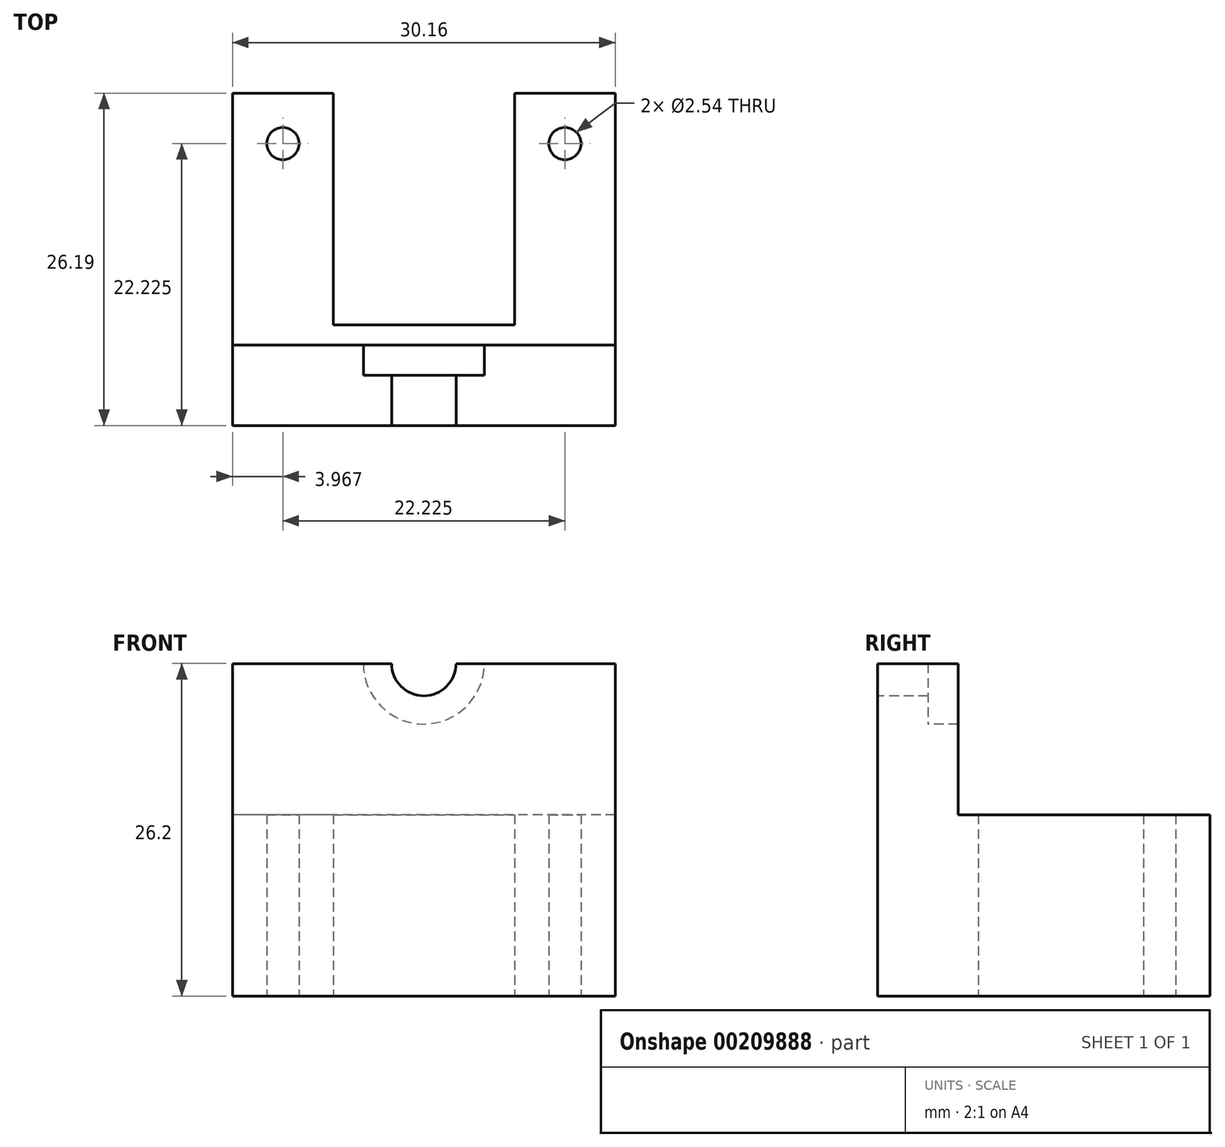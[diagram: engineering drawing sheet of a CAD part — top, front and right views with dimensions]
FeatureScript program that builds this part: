
annotation { "Feature Type Name" : "Feature", "Feature Type Description" : "" }
export const myFeature = defineFeature(function(context is Context, id is Id, definition is map)
    precondition{}
    {
        {
            var Q0;
            Q0=qCreatedBy(makeId("Top.planeOp"),FACE);
            var sketch = newSketch(context, id + "F0", { "sketchPlane" : qUnion([Q0])});
            skLineSegment(sketch, "E0", {"start": v(0, 0) * mm, "end": v(-15.08, 0) * mm});
            skLineSegment(sketch, "E1", {"start": v(-15.08, 0) * mm, "end": v(-15.08, 26.2) * mm});
            skLineSegment(sketch, "E2", {"start": v(-15.08, 26.2) * mm, "end": v(-7.14, 26.2) * mm});
            skLineSegment(sketch, "E3", {"start": v(-7.14, 26.2) * mm, "end": v(-7.14, 7.94) * mm});
            skLineSegment(sketch, "E4", {"start": v(-7.14, 7.94) * mm, "end": v(0, 7.94) * mm});
            skLineSegment(sketch, "E5.MirrorCS", {"start": v(15.08, 26.2) * mm, "end": v(7.14, 26.2) * mm});
            skLineSegment(sketch, "E6.MirrorCS", {"start": v(0, 0) * mm, "end": v(15.08, 0) * mm});
            skLineSegment(sketch, "E7.MirrorCS", {"start": v(7.14, 7.94) * mm, "end": v(0, 7.94) * mm});
            skLineSegment(sketch, "E8.MirrorCS", {"start": v(15.08, 0) * mm, "end": v(15.08, 26.2) * mm});
            skLineSegment(sketch, "E9.MirrorCS", {"start": v(7.14, 26.2) * mm, "end": v(7.14, 7.94) * mm});
            skLineSegment(sketch, "E10", {"start": v(-11.11, 26.2) * mm, "end": v(-11.11, 0) * mm, "construction": true});
            skCircle(sketch, "E11", {"center": v(-11.11, 22.23) * mm, "radius": 1.27 * mm});
            skCircle(sketch, "E12.MirrorC", {"center": v(11.11, 22.23) * mm, "radius": 1.27 * mm});
            skSolve(sketch);
        }
        {
            var Q0;
            Q0=makeQuery(id+"F0.imprint","IMPRINT",FACE,{"disambiguationData":[TD([[makeQuery(id+"F0.imprint","IMPRINT",EDGE,{"derivedFrom":sQuery(id+"F0.wireOp",EDGE,"E0")}),-1.0]])]});
            extrude(context, id + "F1", {"entities" : qUnion([Q0]), "endBound" : BoundingType.SYMMETRIC, "depth" : 26.2 * mm});
        }
        {
            var Q0;
            Q0=makeQuery(id+"F1.opExtrude","SWEPT_FACE",FACE,{"disambiguationData":[OSD([sQuery(id+"F0.wireOp",EDGE,"E1")])]});
            var sketch = newSketch(context, id + "F2", { "sketchPlane" : qUnion([Q0])});
            skLineSegment(sketch, "E13.bottom", {"start": v(-26.2, 13.1) * mm, "end": v(-6.35, 13.1) * mm});
            skLineSegment(sketch, "E13.top", {"start": v(-26.2, 1.2) * mm, "end": v(-6.35, 1.2) * mm});
            skLineSegment(sketch, "E13.left", {"start": v(-26.2, 13.1) * mm, "end": v(-26.2, 1.2) * mm});
            skLineSegment(sketch, "E13.right", {"start": v(-6.35, 13.1) * mm, "end": v(-6.35, 1.2) * mm});
            skSolve(sketch);
        }
        {
            var Q0;
            Q0=makeQuery(id+"F2.imprint","IMPRINT",FACE,{"disambiguationData":[TD([[makeQuery(id+"F2.imprint","IMPRINT",EDGE,{"derivedFrom":sQuery(id+"F2.wireOp",EDGE,"E13.bottom")}),1.0]])]});
            extrude(context, id + "F3", {"entities" : qUnion([Q0]), "operationType" : NewBodyOperationType.REMOVE, "endBound" : BoundingType.THROUGH_ALL, "oppositeDirection" : true, "depth" : 25.4 * mm});
        }
        {
            var Q0;
            Q0=makeQuery(id+"F1.opExtrude","SWEPT_FACE",FACE,{"disambiguationData":[OSD([sQuery(id+"F0.wireOp",EDGE,"E0"),sQuery(id+"F0.wireOp",EDGE,"E6.MirrorCS")])]});
            var sketch = newSketch(context, id + "F4", { "sketchPlane" : qUnion([Q0])});
            skCircle(sketch, "E14", {"center": v(0, 13.1) * mm, "radius": 2.54 * mm});
            skSolve(sketch);
        }
        {
            var Q0;
            {var subQ0=sQuery(id+"F4.wireOp",EDGE,"E14");var subQ1=makeQuery(id+"F1.opExtrude","CAP_EDGE",EDGE,{"disambiguationData":[OSD([sQuery(id+"F0.wireOp",EDGE,"E0"),sQuery(id+"F0.wireOp",EDGE,"E6.MirrorCS")])],"isStart":false});var subQ2=makeQuery(id+"F4.imprint","INTERSECT",VERTEX,{"disambiguationData":[OD(0.0)],"derivedFrom":[subQ1,subQ0]});Q0=makeQuery(id+"F4.imprint","IMPRINT",FACE,{"disambiguationData":[TD([[makeQuery(id+"F4.imprint","IMPRINT",EDGE,{"disambiguationData":[TD([[subQ2,-1.0]])],"derivedFrom":subQ0}),1.0]])]});}
            extrude(context, id + "F5", {"entities" : qUnion([Q0]), "operationType" : NewBodyOperationType.REMOVE, "endBound" : BoundingType.THROUGH_ALL, "oppositeDirection" : true, "depth" : 25.4 * mm});
        }
        {
            var Q0;
            Q0=makeQuery(id+"F1.opExtrude","SWEPT_FACE",FACE,{"disambiguationData":[OSD([sQuery(id+"F0.wireOp",EDGE,"E5.MirrorCS")])]});
            cPlane(context, id + "F6", {"entities" : qUnion([Q0]), "cplaneType" : CPlaneType.OFFSET, "offset" : 22.22 * mm, "oppositeDirection" : true, "width" : 152.4 * mm, "height" : 152.4 * mm});
        }
        {
            var Q0;
            Q0=qCreatedBy(id+"F6.planeOp",FACE);
            var sketch = newSketch(context, id + "F7", { "sketchPlane" : qUnion([Q0])});
            skCircle(sketch, "E15", {"center": v(0, 13.1) * mm, "radius": 4.76 * mm});
            skSolve(sketch);
        }
        {
            var Q0;
            Q0=makeQuery(id+"F7.imprint","IMPRINT",FACE,{"disambiguationData":[TD([[makeQuery(id+"F7.imprint","IMPRINT",EDGE,{"derivedFrom":sQuery(id+"F7.wireOp",EDGE,"E15")}),1.0]])]});
            extrude(context, id + "F8", {"entities" : qUnion([Q0]), "operationType" : NewBodyOperationType.REMOVE, "endBound" : BoundingType.THROUGH_ALL, "depth" : 25.4 * mm});
        }
    });
